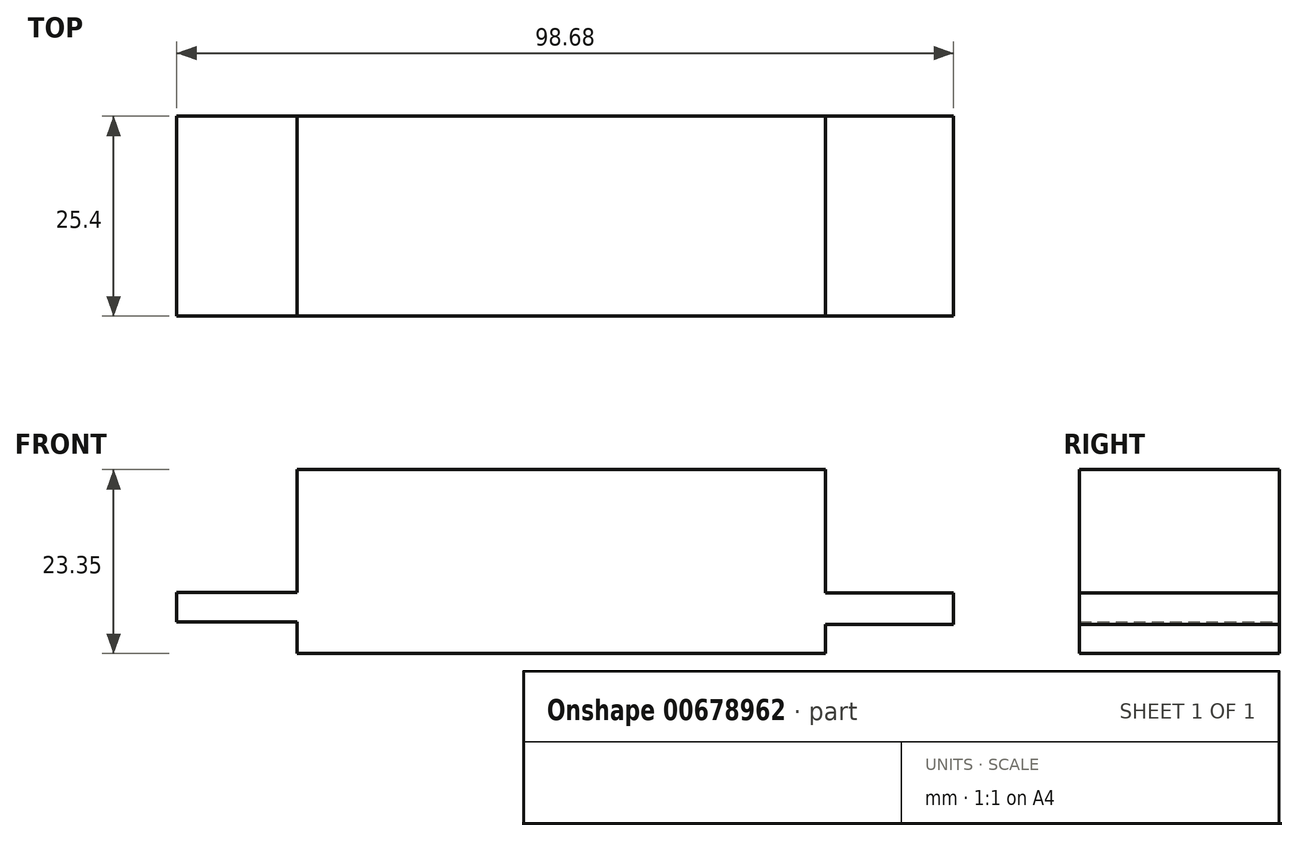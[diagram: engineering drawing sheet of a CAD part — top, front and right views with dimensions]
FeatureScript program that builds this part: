
annotation { "Feature Type Name" : "Feature", "Feature Type Description" : "" }
export const myFeature = defineFeature(function(context is Context, id is Id, definition is map)
    precondition{}
    {
        {
            var Q0;
            Q0=qCreatedBy(makeId("Front.planeOp"),FACE);
            var sketch = newSketch(context, id + "F0", { "sketchPlane" : qUnion([Q0])});
            skLineSegment(sketch, "E0.bottom", {"start": v(-50.36, 48.03) * mm, "end": v(16.79, 48.03) * mm});
            skLineSegment(sketch, "E0.top", {"start": v(-50.36, 24.68) * mm, "end": v(16.79, 24.68) * mm});
            skLineSegment(sketch, "E0.left", {"start": v(-50.36, 48.03) * mm, "end": v(-50.36, 24.68) * mm});
            skLineSegment(sketch, "E0.right", {"start": v(16.79, 48.03) * mm, "end": v(16.79, 24.68) * mm});
            skLineSegment(sketch, "E1.bottom", {"start": v(-65.62, 28.7) * mm, "end": v(-50.36, 28.7) * mm});
            skLineSegment(sketch, "E1.top", {"start": v(-65.62, 32.44) * mm, "end": v(-50.36, 32.44) * mm});
            skLineSegment(sketch, "E1.left", {"start": v(-65.62, 28.7) * mm, "end": v(-65.62, 32.44) * mm});
            skLineSegment(sketch, "E1.right", {"start": v(-50.36, 28.7) * mm, "end": v(-50.36, 32.44) * mm});
            skLineSegment(sketch, "E2.bottom", {"start": v(16.79, 32.34) * mm, "end": v(33.06, 32.34) * mm});
            skLineSegment(sketch, "E2.top", {"start": v(16.79, 28.37) * mm, "end": v(33.06, 28.37) * mm});
            skLineSegment(sketch, "E2.left", {"start": v(16.79, 32.34) * mm, "end": v(16.79, 28.37) * mm});
            skLineSegment(sketch, "E2.right", {"start": v(33.06, 32.34) * mm, "end": v(33.06, 28.37) * mm});
            skSolve(sketch);
        }
        {
            var Q0;
            {var subQ3=sQuery(id+"F0.wireOp",EDGE,"E0.bottom");Q0=makeQuery(id+"F0.imprint","IMPRINT",FACE,{"disambiguationData":[TD([[makeQuery(id+"F0.imprint","IMPRINT",EDGE,{"derivedFrom":subQ3}),-1.0]])]});}
            var Q1;
            Q1=makeQuery(id+"F0.imprint","IMPRINT",FACE,{"disambiguationData":[TD([[makeQuery(id+"F0.imprint","IMPRINT",EDGE,{"derivedFrom":sQuery(id+"F0.wireOp",EDGE,"E2.bottom")}),-1.0]])]});
            var Q2;
            Q2=makeQuery(id+"F0.imprint","IMPRINT",FACE,{"disambiguationData":[TD([[makeQuery(id+"F0.imprint","IMPRINT",EDGE,{"derivedFrom":sQuery(id+"F0.wireOp",EDGE,"E1.bottom")}),1.0]])]});
            extrude(context, id + "F1", {"entities" : qUnion([Q0, Q1, Q2]), "depth" : 25.4 * mm, "offsetDistance" : 25.4 * mm});
        }
    });
